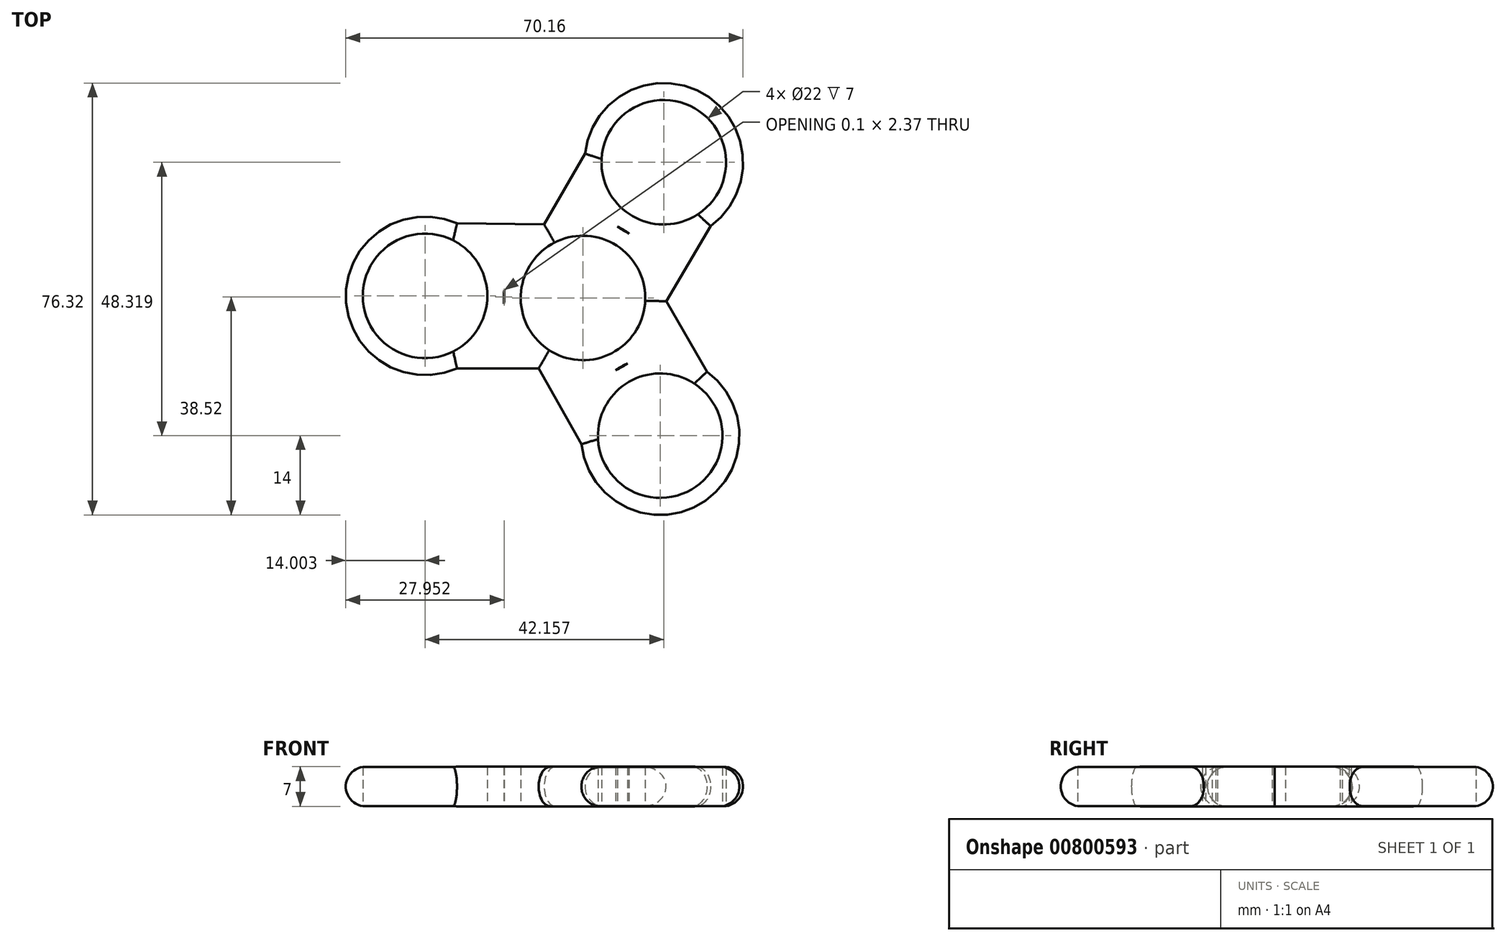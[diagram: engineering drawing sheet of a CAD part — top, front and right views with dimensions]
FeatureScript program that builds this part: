
annotation { "Feature Type Name" : "Feature", "Feature Type Description" : "" }
export const myFeature = defineFeature(function(context is Context, id is Id, definition is map)
    precondition{}
    {
        {
            var Q0;
            Q0=qCreatedBy(makeId("Top.planeOp"),FACE);
            var sketch = newSketch(context, id + "F0", { "sketchPlane" : qUnion([Q0])});
            skCircle(sketch, "E0", {"center": v(0, 0) * mm, "radius": 14 * mm});
            skCircle(sketch, "E1", {"center": v(0, 0) * mm, "radius": 11 * mm});
            skCircle(sketch, "E2", {"center": v(-27.9, 0.36) * mm, "radius": 14 * mm});
            skCircle(sketch, "E3", {"center": v(-27.9, 0.36) * mm, "radius": 11 * mm});
            skLineSegment(sketch, "E4", {"start": v(-6.4, -12.45) * mm, "end": v(-22.26, -12.45) * mm});
            skLineSegment(sketch, "E5", {"start": v(-22.26, 13.17) * mm, "end": v(-5.21, 13) * mm});
            skPoint(sketch, "E6.end.orphan", {"position": v(1.67, 23.77) * mm});
            skPoint(sketch, "E7.center.orphan", {"position": v(15.67, 23.77) * mm});
            skPoint(sketch, "E8.start.orphan", {"position": v(14, 0) * mm});
            skCircle(sketch, "E9.1.0", {"center": v(13.64, -24.34) * mm, "radius": 14 * mm});
            skLineSegment(sketch, "E9.1.1", {"start": v(13.98, 0.69) * mm, "end": v(21.91, -13.05) * mm});
            skLineSegment(sketch, "E9.1.2", {"start": v(-0.28, -25.86) * mm, "end": v(-8.65, -11.01) * mm});
            skCircle(sketch, "E9.1.3", {"center": v(13.64, -24.34) * mm, "radius": 11 * mm});
            skCircle(sketch, "E9.2.0", {"center": v(14.26, 23.98) * mm, "radius": 14 * mm});
            skLineSegment(sketch, "E9.2.1", {"start": v(-7.59, 11.77) * mm, "end": v(0.34, 25.5) * mm});
            skLineSegment(sketch, "E9.2.2", {"start": v(22.54, 12.69) * mm, "end": v(13.86, -1.98) * mm});
            skCircle(sketch, "E9.2.3", {"center": v(14.26, 23.98) * mm, "radius": 11 * mm});
            skSolve(sketch);
        }
        {
            var Q0;
            Q0=makeQuery(id+"F0.imprint","IMPRINT",FACE,{"disambiguationData":[TD([[makeQuery(id+"F0.imprint","IMPRINT",EDGE,{"derivedFrom":sQuery(id+"F0.wireOp",EDGE,"E0")}),1.0]])]});
            extrude(context, id + "F1", {"entities" : qUnion([Q0]), "depth" : 7 * mm, "offsetDistance" : 25 * mm});
        }
        {
            var Q0;
            Q0 = qSketchRegion(id + "F0", true);
            extrude(context, id + "F2", {"entities" : qUnion([Q0]), "operationType" : NewBodyOperationType.ADD, "depth" : 7 * mm, "offsetDistance" : 25 * mm});
        }
        {
            var Q0;
            Q0=makeQuery(id+"F2.opExtrude","CAP_EDGE",EDGE,{"disambiguationData":[OSD([sQuery(id+"F0.wireOp",EDGE,"E6")])],"isStart":false});
            var Q1;
            Q1=makeQuery(id+"F2.opExtrude","CAP_EDGE",EDGE,{"disambiguationData":[OSD([sQuery(id+"F0.wireOp",EDGE,"24565d08-ae06-4ca8-bc44-d6e0c9719509")])],"isStart":false});
            var Q2;
            Q2=makeQuery(id+"F2.opExtrude","CAP_EDGE",EDGE,{"disambiguationData":[OSD([sQuery(id+"F0.wireOp",EDGE,"21nd1R9n-JM8x-KKdz-UYoK-UywRCYNUTJlj")])],"isStart":false});
            var Q3;
            Q3=makeQuery(id+"F2.opExtrude","CAP_EDGE",EDGE,{"disambiguationData":[OSD([sQuery(id+"F0.wireOp",EDGE,"E8")])],"isStart":false});
            var Q4;
            Q4=makeQuery(id+"F2.opExtrude","CAP_EDGE",EDGE,{"disambiguationData":[OSD([sQuery(id+"F0.wireOp",EDGE,"c437219f-0876-4246-bcd2-0642395e3f02")])],"isStart":false});
            var Q5;
            Q5=makeQuery(id+"F2.opExtrude","CAP_EDGE",EDGE,{"disambiguationData":[OSD([sQuery(id+"F0.wireOp",EDGE,"zYvWZh9w-RUU8-ypZr-6T6W-TyqVYuzbnXXZ")])],"isStart":false});
            var Q6;
            Q6=makeQuery(id+"F2.opExtrude","CAP_EDGE",EDGE,{"disambiguationData":[OSD([sQuery(id+"F0.wireOp",EDGE,"E4")])],"isStart":false});
            var Q7;
            {var subQ0=sQuery(id+"F0.wireOp",EDGE,"E2");Q7=makeQuery(id+"F2.opExtrude","CAP_EDGE",EDGE,{"disambiguationData":[OSD([subQ0]),TDD([makeQuery(id+"F0.imprint","IMPRINT",EDGE,{"disambiguationData":[TD([[makeQuery(id+"F0.imprint","INTERSECT",VERTEX,{"derivedFrom":[subQ0,sQuery(id+"F0.wireOp",EDGE,"E4")]}),1.0]])],"derivedFrom":subQ0})])],"isStart":false});}
            var Q8;
            Q8=makeQuery(id+"F2.opExtrude","CAP_EDGE",EDGE,{"disambiguationData":[OSD([sQuery(id+"F0.wireOp",EDGE,"E5")])],"isStart":false});
            var Q9;
            Q9=makeQuery(id+"F2.opExtrude","CAP_EDGE",EDGE,{"disambiguationData":[OSD([sQuery(id+"F0.wireOp",EDGE,"c437219f-0876-4246-bcd2-0642395e3f02")])],"isStart":true});
            var Q10;
            Q10=makeQuery(id+"F2.opExtrude","CAP_EDGE",EDGE,{"disambiguationData":[OSD([sQuery(id+"F0.wireOp",EDGE,"zYvWZh9w-RUU8-ypZr-6T6W-TyqVYuzbnXXZ")])],"isStart":true});
            var Q11;
            Q11=makeQuery(id+"F2.opExtrude","CAP_EDGE",EDGE,{"disambiguationData":[OSD([sQuery(id+"F0.wireOp",EDGE,"E8")])],"isStart":true});
            var Q12;
            Q12=makeQuery(id+"F2.opExtrude","CAP_EDGE",EDGE,{"disambiguationData":[OSD([sQuery(id+"F0.wireOp",EDGE,"21nd1R9n-JM8x-KKdz-UYoK-UywRCYNUTJlj")])],"isStart":true});
            var Q13;
            Q13=makeQuery(id+"F2.opExtrude","CAP_EDGE",EDGE,{"disambiguationData":[OSD([sQuery(id+"F0.wireOp",EDGE,"24565d08-ae06-4ca8-bc44-d6e0c9719509")])],"isStart":true});
            var Q14;
            Q14=makeQuery(id+"F2.opExtrude","CAP_EDGE",EDGE,{"disambiguationData":[OSD([sQuery(id+"F0.wireOp",EDGE,"E6")])],"isStart":true});
            var Q15;
            Q15=makeQuery(id+"F2.opExtrude","CAP_EDGE",EDGE,{"disambiguationData":[OSD([sQuery(id+"F0.wireOp",EDGE,"E5")])],"isStart":true});
            var Q16;
            {var subQ0=sQuery(id+"F0.wireOp",EDGE,"E2");Q16=makeQuery(id+"F2.opExtrude","CAP_EDGE",EDGE,{"disambiguationData":[OSD([subQ0]),TDD([makeQuery(id+"F0.imprint","IMPRINT",EDGE,{"disambiguationData":[TD([[makeQuery(id+"F0.imprint","INTERSECT",VERTEX,{"derivedFrom":[subQ0,sQuery(id+"F0.wireOp",EDGE,"E4")]}),1.0]])],"derivedFrom":subQ0})])],"isStart":true});}
            var Q17;
            Q17=makeQuery(id+"F2.opExtrude","CAP_EDGE",EDGE,{"disambiguationData":[OSD([sQuery(id+"F0.wireOp",EDGE,"E4")])],"isStart":true});
            var Q18;
            Q18=makeQuery(id+"F2.opExtrude","CAP_EDGE",EDGE,{"disambiguationData":[OSD([sQuery(id+"F0.wireOp",EDGE,"oPU3L3Sa-onpL-B134-E07B-53HArGgJh5Kt")])],"isStart":false});
            var Q19;
            Q19=makeQuery(id+"F2.opExtrude","CAP_EDGE",EDGE,{"disambiguationData":[OSD([sQuery(id+"F0.wireOp",EDGE,"oPU3L3Sa-onpL-B134-E07B-53HArGgJh5Kt")])],"isStart":true});
            fillet(context, id + "F3", {"entities" : qUnion([Q0, Q1, Q2, Q3, Q4, Q5, Q6, Q7, Q8, Q9, Q10, Q11, Q12, Q13, Q14, Q15, Q16, Q17, Q18, Q19]), "radius" : 3.5 * mm, "tangentPropagation" : true, "allowEdgeOverflow" : false});
        }
        {
            var Q0;
            Q0=makeQuery(id+"F2.opExtrude","CAP_EDGE",EDGE,{"disambiguationData":[OSD([sQuery(id+"F0.wireOp",EDGE,"E9.1.2")])],"isStart":false});
            var Q1;
            Q1=makeQuery(id+"F2.opExtrude","CAP_EDGE",EDGE,{"disambiguationData":[OSD([sQuery(id+"F0.wireOp",EDGE,"E9.1.2")])],"isStart":true});
            var Q2;
            Q2=makeQuery(id+"F2.opExtrude","CAP_EDGE",EDGE,{"disambiguationData":[OSD([sQuery(id+"F0.wireOp",EDGE,"E9.1.0")])],"isStart":false});
            var Q3;
            Q3=makeQuery(id+"F2.opExtrude","CAP_EDGE",EDGE,{"disambiguationData":[OSD([sQuery(id+"F0.wireOp",EDGE,"E9.1.0")])],"isStart":true});
            var Q4;
            Q4=makeQuery(id+"F2.opExtrude","CAP_EDGE",EDGE,{"disambiguationData":[OSD([sQuery(id+"F0.wireOp",EDGE,"E9.1.1")])],"isStart":false});
            var Q5;
            Q5=makeQuery(id+"F2.opExtrude","CAP_EDGE",EDGE,{"disambiguationData":[OSD([sQuery(id+"F0.wireOp",EDGE,"E9.2.2")])],"isStart":false});
            var Q6;
            Q6=makeQuery(id+"F2.opExtrude","CAP_EDGE",EDGE,{"disambiguationData":[OSD([sQuery(id+"F0.wireOp",EDGE,"E9.2.2")])],"isStart":true});
            var Q7;
            Q7=makeQuery(id+"F2.opExtrude","CAP_EDGE",EDGE,{"disambiguationData":[OSD([sQuery(id+"F0.wireOp",EDGE,"E9.1.1")])],"isStart":true});
            var Q8;
            Q8=makeQuery(id+"F2.opExtrude","CAP_EDGE",EDGE,{"disambiguationData":[OSD([sQuery(id+"F0.wireOp",EDGE,"E9.2.0")])],"isStart":false});
            var Q9;
            Q9=makeQuery(id+"F2.opExtrude","CAP_EDGE",EDGE,{"disambiguationData":[OSD([sQuery(id+"F0.wireOp",EDGE,"E9.2.0")])],"isStart":true});
            var Q10;
            Q10=makeQuery(id+"F2.opExtrude","CAP_EDGE",EDGE,{"disambiguationData":[OSD([sQuery(id+"F0.wireOp",EDGE,"E9.2.1")])],"isStart":false});
            var Q11;
            Q11=makeQuery(id+"F2.opExtrude","CAP_EDGE",EDGE,{"disambiguationData":[OSD([sQuery(id+"F0.wireOp",EDGE,"E9.2.1")])],"isStart":true});
            fillet(context, id + "F4", {"entities" : qUnion([Q0, Q1, Q2, Q3, Q4, Q5, Q6, Q7, Q8, Q9, Q10, Q11]), "radius" : 3.5 * mm, "tangentPropagation" : true, "allowEdgeOverflow" : false});
        }
    });
